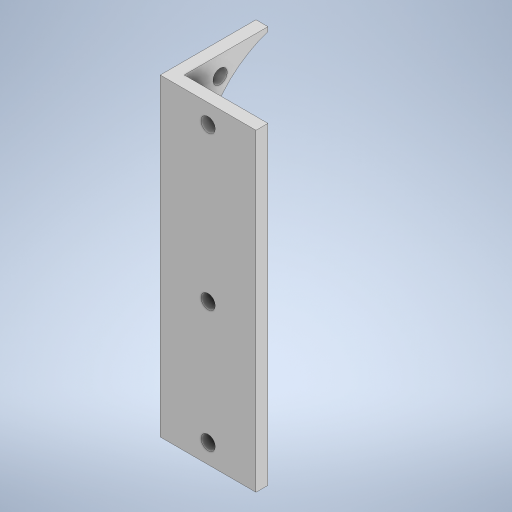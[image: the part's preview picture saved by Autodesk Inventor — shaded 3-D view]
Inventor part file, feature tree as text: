
AUTODESK INVENTOR PART (.ipt)
format: ipt  version: 2023 (Build 270158000, 158)  size: 292,352 bytes
history: native  units: in
note: dims shown in document units (in); Inventor stores cm internally (conversion verified against a paired STEP export)
features: extrude x3, mirror x2, sketch x1
ambient origin geometry x8: Origin, YZ Plane, XZ Plane, XY Plane, X Axis, Y Axis, Z Axis, Center Point
bodies: Solid2 (feature_tree)
feature tree (6):
  extrude  "Extrusion3"  Depth=0.125in
  extrude  "Extrusion4"  Depth=0.125in TaperAngle=0.0deg
  extrude  "Extrusion5"  Depth=1.0in TaperAngle=0.0deg
  mirror  "Mirror1"
  mirror  "Mirror2"
  sketch  "Sketch3"  dims[d16=0.15in d41=0.125in d42=0.125in d43=0.0in d44=1.0in d45=0.0in d46=0.15in d47=0.15in d48=0.15in d49=1.0in d50=0.0in d51=0.15in d52=0.15in]
